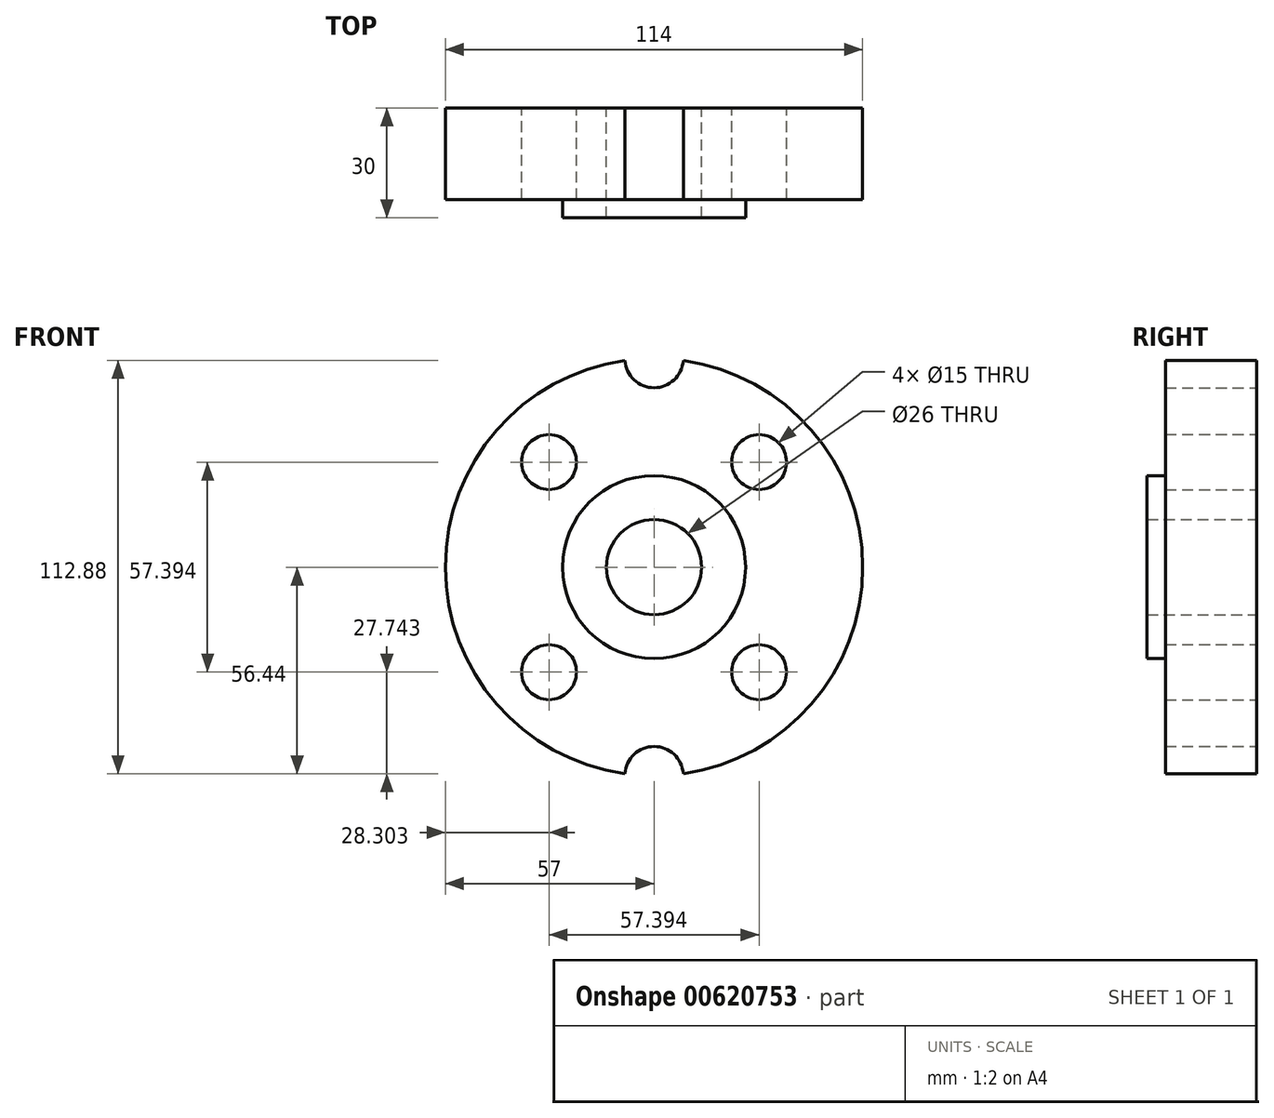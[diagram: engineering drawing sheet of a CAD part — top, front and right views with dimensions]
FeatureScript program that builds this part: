
annotation { "Feature Type Name" : "Feature", "Feature Type Description" : "" }
export const myFeature = defineFeature(function(context is Context, id is Id, definition is map)
    precondition{}
    {
        {
            var Q0;
            Q0=qCreatedBy(makeId("Front.planeOp"),FACE);
            var sketch = newSketch(context, id + "F0", { "sketchPlane" : qUnion([Q0])});
            skCircle(sketch, "E0", {"center": v(0, 0) * mm, "radius": 13 * mm});
            skArc(sketch, "E1", {"start": v(-7.98, 56.44) * mm, "mid": v(-57, 0) * mm, "end": v(-7.98, -56.44) * mm});
            skLineSegment(sketch, "E2", {"start": v(-71.04, 0) * mm, "end": v(-57, 0) * mm});
            skCircle(sketch, "E3", {"center": v(0, 0) * mm, "radius": 25 * mm});
            skCircle(sketch, "E4", {"center": v(28.7, 28.7) * mm, "radius": 7.5 * mm});
            skCircle(sketch, "E5", {"center": v(-28.7, 28.7) * mm, "radius": 7.5 * mm});
            skCircle(sketch, "E6", {"center": v(-28.7, -28.7) * mm, "radius": 7.5 * mm});
            skCircle(sketch, "E7", {"center": v(28.7, -28.7) * mm, "radius": 7.5 * mm});
            skArc(sketch, "E8", {"start": v(-7.98, 56.44) * mm, "mid": v(0, 49) * mm, "end": v(7.98, 56.44) * mm});
            skArc(sketch, "E9", {"start": v(7.98, -56.44) * mm, "mid": v(0, -49) * mm, "end": v(-7.98, -56.44) * mm});
            skPoint(sketch, "E10.orphan", {"position": v(0, 69.51) * mm});
            skLineSegment(sketch, "E11.trimOffspring", {"start": v(57, 0) * mm, "end": v(71.05, 0) * mm});
            skLineSegment(sketch, "E12.trimOffspring", {"start": v(0, -25) * mm, "end": v(0, -49) * mm});
            skPoint(sketch, "E13.trimOffspring.end.orphan", {"position": v(0, -67.64) * mm});
            skArc(sketch, "E14.trimOffspring", {"start": v(7.98, -56.44) * mm, "mid": v(57, 0) * mm, "end": v(7.98, 56.44) * mm});
            skSolve(sketch);
        }
        {
            var Q0;
            Q0=makeQuery(id+"F0.imprint","IMPRINT",FACE,{"disambiguationData":[TD([[makeQuery(id+"F0.imprint","IMPRINT",EDGE,{"derivedFrom":sQuery(id+"F0.wireOp",EDGE,"E3")}),-1.0]])]});
            extrude(context, id + "F1", {"entities" : qUnion([Q0]), "depth" : 25 * mm, "offsetDistance" : 25 * mm});
        }
        {
            var Q0;
            Q0=makeQuery(id+"F0.imprint","IMPRINT",FACE,{"disambiguationData":[TD([[makeQuery(id+"F0.imprint","IMPRINT",EDGE,{"derivedFrom":sQuery(id+"F0.wireOp",EDGE,"E0")}),-1.0]])]});
            extrude(context, id + "F2", {"entities" : qUnion([Q0]), "operationType" : NewBodyOperationType.ADD, "depth" : 30 * mm, "offsetDistance" : 25 * mm});
        }
    });
